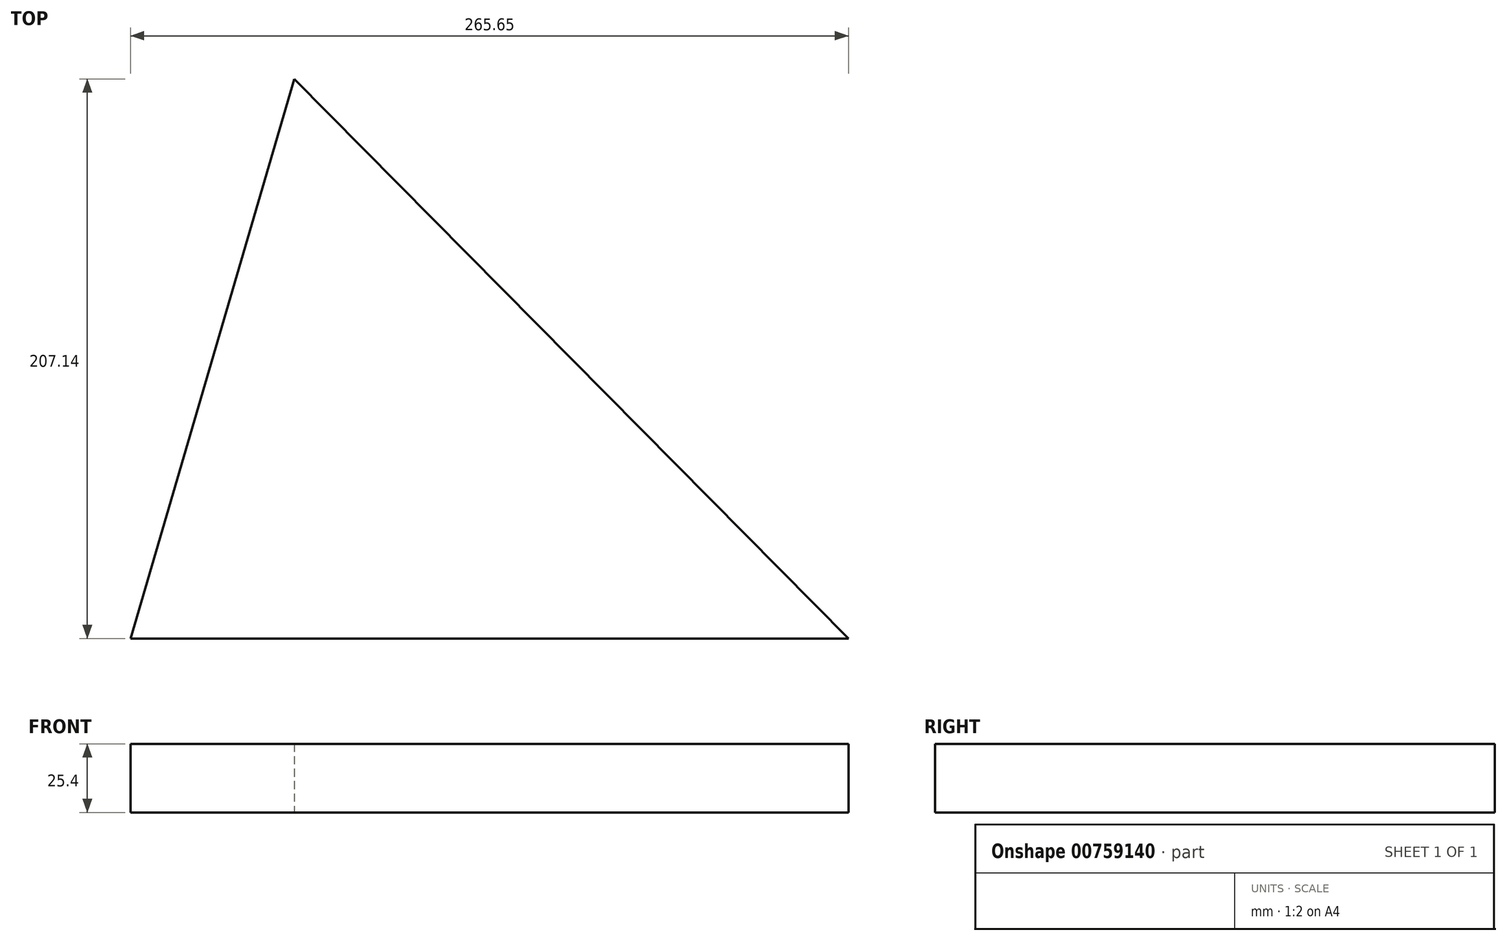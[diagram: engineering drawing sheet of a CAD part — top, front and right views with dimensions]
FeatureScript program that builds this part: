
annotation { "Feature Type Name" : "Feature", "Feature Type Description" : "" }
export const myFeature = defineFeature(function(context is Context, id is Id, definition is map)
    precondition{}
    {
        {
            var Q0;
            Q0=qCreatedBy(makeId("Top.planeOp"),FACE);
            var sketch = newSketch(context, id + "F0", { "sketchPlane" : qUnion([Q0])});
            skLineSegment(sketch, "E0", {"start": v(0, 0) * mm, "end": v(-60.55, -207.14) * mm});
            skLineSegment(sketch, "E1", {"start": v(0, 0) * mm, "end": v(205.1, -207.14) * mm});
            skLineSegment(sketch, "E2", {"start": v(-60.55, -207.14) * mm, "end": v(205.1, -207.14) * mm});
            skLineSegment(sketch, "E3", {"start": v(-60.55, -207.14) * mm, "end": v(136.02, -564.9) * mm});
            skLineSegment(sketch, "E4", {"start": v(136.02, -564.9) * mm, "end": v(350.08, -465.28) * mm});
            skLineSegment(sketch, "E5", {"start": v(214.26, -207.14) * mm, "end": v(350.08, -193.5) * mm});
            skLineSegment(sketch, "E6", {"start": v(350.08, -193.5) * mm, "end": v(350.08, -465.28) * mm});
            skSolve(sketch);
        }
        {
            var Q0;
            Q0=makeQuery(id+"F0.imprint","IMPRINT",FACE,{"disambiguationData":[TD([[makeQuery(id+"F0.imprint","IMPRINT",EDGE,{"derivedFrom":sQuery(id+"F0.wireOp",EDGE,"E0")}),1.0]])]});
            extrude(context, id + "F1", {"entities" : qUnion([Q0]), "depth" : 25.4 * mm, "offsetDistance" : 25.4 * mm});
        }
    });
